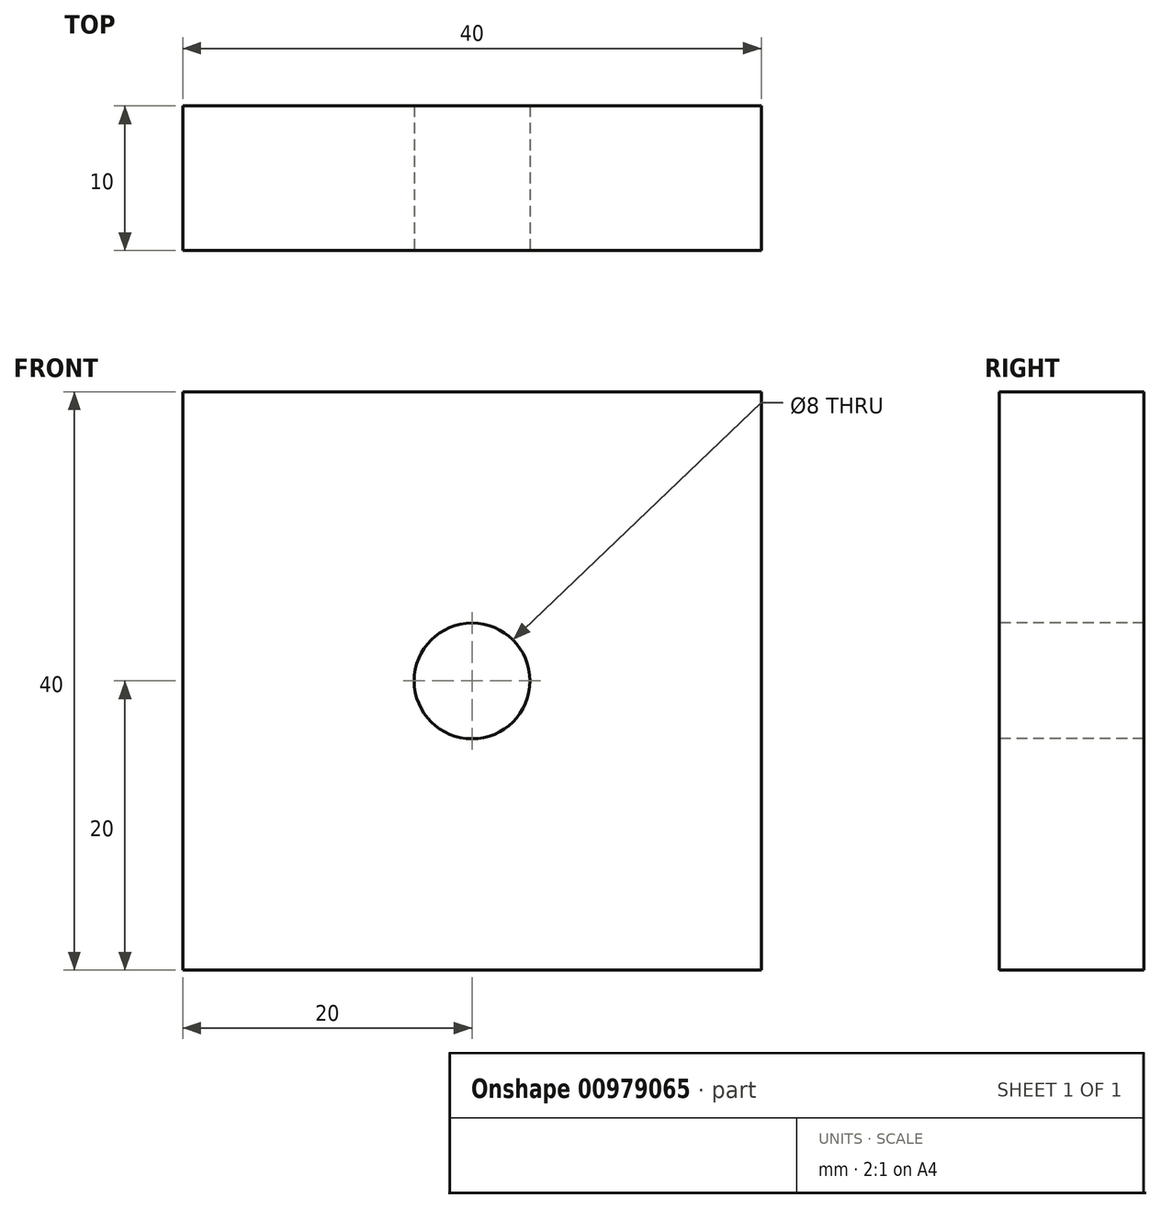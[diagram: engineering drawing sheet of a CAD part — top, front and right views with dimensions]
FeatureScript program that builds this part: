
annotation { "Feature Type Name" : "Feature", "Feature Type Description" : "" }
export const myFeature = defineFeature(function(context is Context, id is Id, definition is map)
    precondition{}
    {
        {
            var Q0;
            Q0=qCreatedBy(makeId("Front.planeOp"),FACE);
            var sketch = newSketch(context, id + "F0", { "sketchPlane" : qUnion([Q0])});
            skLineSegment(sketch, "E0.bottom", {"start": v(0, 0) * mm, "end": v(40, 0) * mm});
            skLineSegment(sketch, "E0.top", {"start": v(0, 40) * mm, "end": v(40, 40) * mm});
            skLineSegment(sketch, "E0.left", {"start": v(0, 0) * mm, "end": v(0, 40) * mm});
            skLineSegment(sketch, "E0.right", {"start": v(40, 0) * mm, "end": v(40, 40) * mm});
            skSolve(sketch);
        }
        {
            var Q0;
            Q0=makeQuery(id+"F0.imprint","IMPRINT",FACE,{"disambiguationData":[TD([[makeQuery(id+"F0.imprint","IMPRINT",EDGE,{"derivedFrom":sQuery(id+"F0.wireOp",EDGE,"E0.bottom")}),1.0]])]});
            extrude(context, id + "F1", {"entities" : qUnion([Q0]), "depth" : 10 * mm, "offsetDistance" : 25 * mm});
        }
        {
            var Q0;
            Q0=makeQuery(id+"F1.opExtrude","CAP_FACE",FACE,{"disambiguationData":[OSD([sQuery(id+"F0.wireOp",EDGE,"E0.bottom"),sQuery(id+"F0.wireOp",EDGE,"E0.top"),sQuery(id+"F0.wireOp",EDGE,"E0.left"),sQuery(id+"F0.wireOp",EDGE,"E0.right")])],"isStart":false});
            var sketch = newSketch(context, id + "F2", { "sketchPlane" : qUnion([Q0])});
            skLineSegment(sketch, "E1", {"start": v(0, 40) * mm, "end": v(40, 0) * mm});
            skPoint(sketch, "E2", {"position": v(20, 20) * mm});
            skSolve(sketch);
        }
        {
            var Q0;
            Q0=sQuery(id+"F2.wireOp",VERTEX,"E2");
            var Q1;
            Q1=makeQuery(id+"F1.opExtrude","SWEPT_BODY",BODY,{"disambiguationData":[OSD([sQuery(id+"F0.wireOp",EDGE,"E0.bottom"),sQuery(id+"F0.wireOp",EDGE,"E0.top"),sQuery(id+"F0.wireOp",EDGE,"E0.left"),sQuery(id+"F0.wireOp",EDGE,"E0.right")])]});
            hole(context, id + "F3", {"style" : HoleStyle.SIMPLE, "endStyle" : HoleEndStyle.THROUGH, "holeDiameter" : 8 * mm, "majorDiameter" : 8 * mm, "isTappedThrough" : true, "tappedDepth" : 12 * mm, "tapClearance" : 3, "locations" : qUnion([Q0]), "scope" : qUnion([Q1])});
        }
    });
